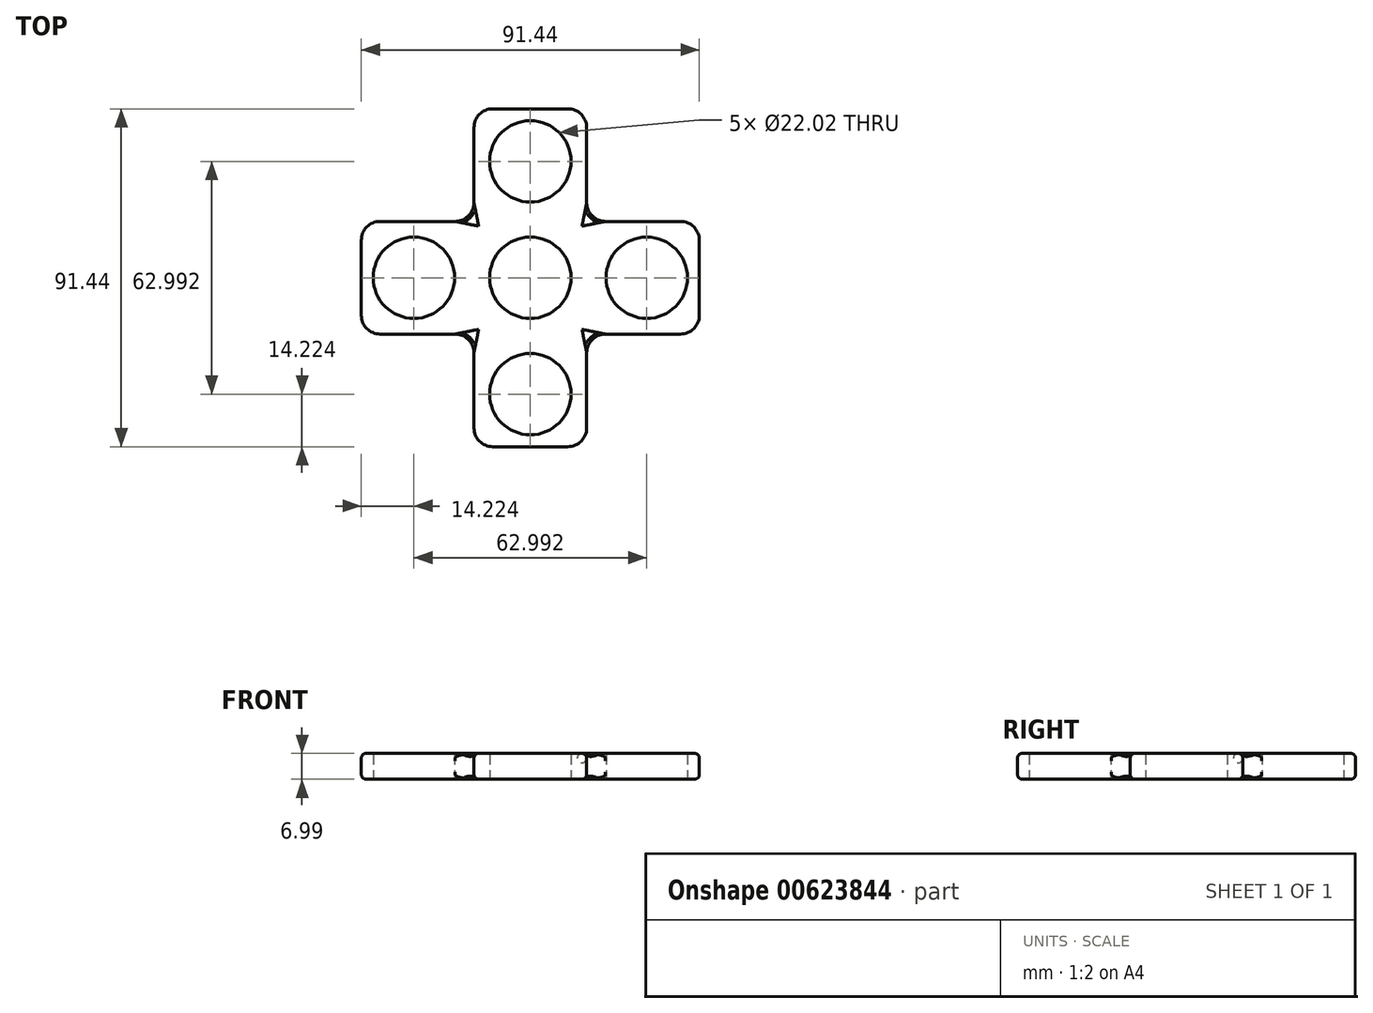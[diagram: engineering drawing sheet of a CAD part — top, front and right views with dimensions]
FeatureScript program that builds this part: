
annotation { "Feature Type Name" : "Feature", "Feature Type Description" : "" }
export const myFeature = defineFeature(function(context is Context, id is Id, definition is map)
    precondition{}
    {
        {
            var Q0;
            Q0=qCreatedBy(makeId("Top.planeOp"),FACE);
            var sketch = newSketch(context, id + "F0", { "sketchPlane" : qUnion([Q0])});
            skCircle(sketch, "E0", {"center": v(0, 0) * mm, "radius": 11.01 * mm});
            skCircle(sketch, "E1", {"center": v(0, 0) * mm, "radius": 18.87 * mm});
            skLineSegment(sketch, "E2", {"start": v(-15.24, 11.13) * mm, "end": v(-15.24, 45.72) * mm});
            skLineSegment(sketch, "E3", {"start": v(-15.24, 45.72) * mm, "end": v(15.24, 45.72) * mm});
            skLineSegment(sketch, "E4", {"start": v(15.24, 45.72) * mm, "end": v(15.24, 11.13) * mm});
            skLineSegment(sketch, "E5.1.0", {"start": v(-45.72, -15.24) * mm, "end": v(-45.72, 15.24) * mm});
            skLineSegment(sketch, "E5.1.1", {"start": v(-11.13, -15.24) * mm, "end": v(-45.72, -15.24) * mm});
            skLineSegment(sketch, "E5.1.2", {"start": v(-45.72, 15.24) * mm, "end": v(-11.13, 15.24) * mm});
            skLineSegment(sketch, "E5.2.0", {"start": v(15.24, -45.72) * mm, "end": v(-15.24, -45.72) * mm});
            skLineSegment(sketch, "E5.2.1", {"start": v(15.24, -11.13) * mm, "end": v(15.24, -45.72) * mm});
            skLineSegment(sketch, "E5.2.2", {"start": v(-15.24, -45.72) * mm, "end": v(-15.24, -11.13) * mm});
            skLineSegment(sketch, "E5.3.0", {"start": v(45.72, 15.24) * mm, "end": v(45.72, -15.24) * mm});
            skLineSegment(sketch, "E5.3.1", {"start": v(11.13, 15.24) * mm, "end": v(45.72, 15.24) * mm});
            skLineSegment(sketch, "E5.3.2", {"start": v(45.72, -15.24) * mm, "end": v(11.13, -15.24) * mm});
            skCircle(sketch, "E6", {"center": v(0, -31.5) * mm, "radius": 11.01 * mm});
            skCircle(sketch, "E7", {"center": v(-31.5, 0) * mm, "radius": 11.01 * mm});
            skCircle(sketch, "E8", {"center": v(31.5, 0) * mm, "radius": 11.01 * mm});
            skCircle(sketch, "E9", {"center": v(0, 31.5) * mm, "radius": 11.01 * mm});
            skLineSegment(sketch, "E10", {"start": v(0, 0) * mm, "end": v(-31.5, 0) * mm});
            skLineSegment(sketch, "E11", {"start": v(0, 0) * mm, "end": v(0, -31.5) * mm});
            skLineSegment(sketch, "E12", {"start": v(0, 0) * mm, "end": v(31.5, 0) * mm});
            skLineSegment(sketch, "E13", {"start": v(0, 0) * mm, "end": v(0, 31.5) * mm});
            skSolve(sketch);
        }
        {
            var Q0;
            Q0 = qSketchRegion(id + "F0", true);
            var Q1;
            {var subQ5=sQuery(id+"F0.wireOp",EDGE,"E0");var subQ7=sQuery(id+"F0.wireOp",EDGE,"E13");var subQ9=makeQuery(id+"F0.imprint","INTERSECT",VERTEX,{"derivedFrom":[subQ5,subQ7]});Q1=makeQuery(id+"F0.imprint","IMPRINT",FACE,{"disambiguationData":[TD([[makeQuery(id+"F0.imprint","IMPRINT",EDGE,{"disambiguationData":[TD([[subQ9,-1.0]])],"derivedFrom":subQ5}),-1.0]])]});}
            var Q2;
            {var subQ2=sQuery(id+"F0.wireOp",EDGE,"E13");var subQ7=sQuery(id+"F0.wireOp",EDGE,"E0");var subQ8=makeQuery(id+"F0.imprint","INTERSECT",VERTEX,{"derivedFrom":[subQ7,subQ2]});Q2=makeQuery(id+"F0.imprint","IMPRINT",FACE,{"disambiguationData":[TD([[makeQuery(id+"F0.imprint","IMPRINT",EDGE,{"disambiguationData":[TD([[subQ8,1.0]])],"derivedFrom":subQ7}),-1.0]])]});}
            var Q3;
            {var subQ2=sQuery(id+"F0.wireOp",EDGE,"E12");var subQ5=sQuery(id+"F0.wireOp",EDGE,"E0");var subQ6=makeQuery(id+"F0.imprint","INTERSECT",VERTEX,{"derivedFrom":[subQ5,subQ2]});Q3=makeQuery(id+"F0.imprint","IMPRINT",FACE,{"disambiguationData":[TD([[makeQuery(id+"F0.imprint","IMPRINT",EDGE,{"disambiguationData":[TD([[subQ6,1.0]])],"derivedFrom":subQ5}),-1.0]])]});}
            var Q4;
            {var subQ3=sQuery(id+"F0.wireOp",EDGE,"E10");var subQ7=sQuery(id+"F0.wireOp",EDGE,"E0");var subQ9=makeQuery(id+"F0.imprint","INTERSECT",VERTEX,{"derivedFrom":[subQ7,subQ3]});Q4=makeQuery(id+"F0.imprint","IMPRINT",FACE,{"disambiguationData":[TD([[makeQuery(id+"F0.imprint","IMPRINT",EDGE,{"disambiguationData":[TD([[subQ9,-1.0]])],"derivedFrom":subQ7}),-1.0]])]});}
            extrude(context, id + "F1", {"entities" : qUnion([Q0, Q1, Q2, Q3, Q4]), "depth" : 7 * mm, "offsetDistance" : 25.4 * mm});
        }
        {
            var Q0;
            Q0=makeQuery(id+"F1.opExtrude","CAP_EDGE",EDGE,{"disambiguationData":[OSD([sQuery(id+"F0.wireOp",EDGE,"E5.2.2")])],"isStart":true});
            var Q1;
            Q1=makeQuery(id+"F1.opExtrude","CAP_EDGE",EDGE,{"disambiguationData":[OSD([sQuery(id+"F0.wireOp",EDGE,"E5.2.0")])],"isStart":true});
            var Q2;
            Q2=makeQuery(id+"F1.opExtrude","CAP_EDGE",EDGE,{"disambiguationData":[OSD([sQuery(id+"F0.wireOp",EDGE,"E5.2.1")])],"isStart":true});
            var Q3;
            Q3=makeQuery(id+"F1.opExtrude","CAP_EDGE",EDGE,{"disambiguationData":[OSD([sQuery(id+"F0.wireOp",EDGE,"E5.3.2")])],"isStart":true});
            var Q4;
            Q4=makeQuery(id+"F1.opExtrude","CAP_EDGE",EDGE,{"disambiguationData":[OSD([sQuery(id+"F0.wireOp",EDGE,"E5.3.0")])],"isStart":true});
            var Q5;
            Q5=makeQuery(id+"F1.opExtrude","CAP_EDGE",EDGE,{"disambiguationData":[OSD([sQuery(id+"F0.wireOp",EDGE,"E5.3.1")])],"isStart":true});
            var Q6;
            Q6=makeQuery(id+"F1.opExtrude","CAP_EDGE",EDGE,{"disambiguationData":[OSD([sQuery(id+"F0.wireOp",EDGE,"E4")])],"isStart":true});
            var Q7;
            Q7=makeQuery(id+"F1.opExtrude","CAP_EDGE",EDGE,{"disambiguationData":[OSD([sQuery(id+"F0.wireOp",EDGE,"E3")])],"isStart":true});
            var Q8;
            Q8=makeQuery(id+"F1.opExtrude","CAP_EDGE",EDGE,{"disambiguationData":[OSD([sQuery(id+"F0.wireOp",EDGE,"E2")])],"isStart":true});
            var Q9;
            Q9=makeQuery(id+"F1.opExtrude","CAP_EDGE",EDGE,{"disambiguationData":[OSD([sQuery(id+"F0.wireOp",EDGE,"E5.1.2")])],"isStart":true});
            var Q10;
            Q10=makeQuery(id+"F1.opExtrude","CAP_EDGE",EDGE,{"disambiguationData":[OSD([sQuery(id+"F0.wireOp",EDGE,"E5.1.0")])],"isStart":true});
            var Q11;
            Q11=makeQuery(id+"F1.opExtrude","CAP_EDGE",EDGE,{"disambiguationData":[OSD([sQuery(id+"F0.wireOp",EDGE,"E5.1.1")])],"isStart":true});
            fillet(context, id + "F2", {"entities" : qUnion([Q0, Q1, Q2, Q3, Q4, Q5, Q6, Q7, Q8, Q9, Q10, Q11]), "radius" : 1.27 * mm, "tangentPropagation" : true, "allowEdgeOverflow" : false});
        }
        {
            var Q0;
            Q0=makeQuery(id+"F1.opExtrude","CAP_EDGE",EDGE,{"disambiguationData":[OSD([sQuery(id+"F0.wireOp",EDGE,"E5.1.0")])],"isStart":false});
            var Q1;
            Q1=makeQuery(id+"F1.opExtrude","CAP_EDGE",EDGE,{"disambiguationData":[OSD([sQuery(id+"F0.wireOp",EDGE,"E5.1.2")])],"isStart":false});
            var Q2;
            Q2=makeQuery(id+"F1.opExtrude","CAP_EDGE",EDGE,{"disambiguationData":[OSD([sQuery(id+"F0.wireOp",EDGE,"E2")])],"isStart":false});
            var Q3;
            Q3=makeQuery(id+"F1.opExtrude","CAP_EDGE",EDGE,{"disambiguationData":[OSD([sQuery(id+"F0.wireOp",EDGE,"E3")])],"isStart":false});
            var Q4;
            Q4=makeQuery(id+"F1.opExtrude","CAP_EDGE",EDGE,{"disambiguationData":[OSD([sQuery(id+"F0.wireOp",EDGE,"E4")])],"isStart":false});
            var Q5;
            Q5=makeQuery(id+"F1.opExtrude","CAP_EDGE",EDGE,{"disambiguationData":[OSD([sQuery(id+"F0.wireOp",EDGE,"E5.3.1")])],"isStart":false});
            var Q6;
            Q6=makeQuery(id+"F1.opExtrude","CAP_EDGE",EDGE,{"disambiguationData":[OSD([sQuery(id+"F0.wireOp",EDGE,"E5.3.0")])],"isStart":false});
            var Q7;
            Q7=makeQuery(id+"F1.opExtrude","CAP_EDGE",EDGE,{"disambiguationData":[OSD([sQuery(id+"F0.wireOp",EDGE,"E5.3.2")])],"isStart":false});
            var Q8;
            Q8=makeQuery(id+"F1.opExtrude","CAP_EDGE",EDGE,{"disambiguationData":[OSD([sQuery(id+"F0.wireOp",EDGE,"E5.2.1")])],"isStart":false});
            var Q9;
            Q9=makeQuery(id+"F1.opExtrude","CAP_EDGE",EDGE,{"disambiguationData":[OSD([sQuery(id+"F0.wireOp",EDGE,"E5.2.0")])],"isStart":false});
            var Q10;
            Q10=makeQuery(id+"F1.opExtrude","CAP_EDGE",EDGE,{"disambiguationData":[OSD([sQuery(id+"F0.wireOp",EDGE,"E5.2.2")])],"isStart":false});
            var Q11;
            Q11=makeQuery(id+"F1.opExtrude","CAP_EDGE",EDGE,{"disambiguationData":[OSD([sQuery(id+"F0.wireOp",EDGE,"E5.1.1")])],"isStart":false});
            fillet(context, id + "F3", {"entities" : qUnion([Q0, Q1, Q2, Q3, Q4, Q5, Q6, Q7, Q8, Q9, Q10, Q11]), "radius" : 1.27 * mm, "tangentPropagation" : true, "allowEdgeOverflow" : false});
        }
        {
            var Q0;
            Q0=makeQuery(id+"F1.opExtrude","SWEPT_EDGE",EDGE,{"disambiguationData":[OSD([sQuery(id+"F0.wireOp",EDGE,"E2"),sQuery(id+"F0.wireOp",EDGE,"E5.1.2")])]});
            var Q1;
            Q1=makeQuery(id+"F1.opExtrude","SWEPT_EDGE",EDGE,{"disambiguationData":[OSD([sQuery(id+"F0.wireOp",EDGE,"E2"),sQuery(id+"F0.wireOp",EDGE,"E3")])]});
            var Q2;
            Q2=makeQuery(id+"F1.opExtrude","SWEPT_EDGE",EDGE,{"disambiguationData":[OSD([sQuery(id+"F0.wireOp",EDGE,"E3"),sQuery(id+"F0.wireOp",EDGE,"E4")])]});
            var Q3;
            Q3=makeQuery(id+"F1.opExtrude","SWEPT_EDGE",EDGE,{"disambiguationData":[OSD([sQuery(id+"F0.wireOp",EDGE,"E5.1.0"),sQuery(id+"F0.wireOp",EDGE,"E5.1.2")])]});
            var Q4;
            Q4=makeQuery(id+"F1.opExtrude","SWEPT_EDGE",EDGE,{"disambiguationData":[OSD([sQuery(id+"F0.wireOp",EDGE,"E5.1.0"),sQuery(id+"F0.wireOp",EDGE,"E5.1.1")])]});
            var Q5;
            Q5=makeQuery(id+"F1.opExtrude","SWEPT_EDGE",EDGE,{"disambiguationData":[OSD([sQuery(id+"F0.wireOp",EDGE,"E5.2.0"),sQuery(id+"F0.wireOp",EDGE,"E5.2.2")])]});
            var Q6;
            Q6=makeQuery(id+"F1.opExtrude","SWEPT_EDGE",EDGE,{"disambiguationData":[OSD([sQuery(id+"F0.wireOp",EDGE,"E5.1.1"),sQuery(id+"F0.wireOp",EDGE,"E5.2.2")])]});
            var Q7;
            Q7=makeQuery(id+"F1.opExtrude","SWEPT_EDGE",EDGE,{"disambiguationData":[OSD([sQuery(id+"F0.wireOp",EDGE,"E5.2.0"),sQuery(id+"F0.wireOp",EDGE,"E5.2.1")])]});
            var Q8;
            Q8=makeQuery(id+"F1.opExtrude","SWEPT_EDGE",EDGE,{"disambiguationData":[OSD([sQuery(id+"F0.wireOp",EDGE,"E5.2.1"),sQuery(id+"F0.wireOp",EDGE,"E5.3.2")])]});
            var Q9;
            Q9=makeQuery(id+"F1.opExtrude","SWEPT_EDGE",EDGE,{"disambiguationData":[OSD([sQuery(id+"F0.wireOp",EDGE,"E5.3.0"),sQuery(id+"F0.wireOp",EDGE,"E5.3.2")])]});
            var Q10;
            Q10=makeQuery(id+"F1.opExtrude","SWEPT_EDGE",EDGE,{"disambiguationData":[OSD([sQuery(id+"F0.wireOp",EDGE,"E5.3.0"),sQuery(id+"F0.wireOp",EDGE,"E5.3.1")])]});
            var Q11;
            Q11=makeQuery(id+"F1.opExtrude","SWEPT_EDGE",EDGE,{"disambiguationData":[OSD([sQuery(id+"F0.wireOp",EDGE,"E4"),sQuery(id+"F0.wireOp",EDGE,"E5.3.1")])]});
            fillet(context, id + "F4", {"entities" : qUnion([Q0, Q1, Q2, Q3, Q4, Q5, Q6, Q7, Q8, Q9, Q10, Q11]), "radius" : 5.08 * mm, "tangentPropagation" : true, "allowEdgeOverflow" : false});
        }
    });
